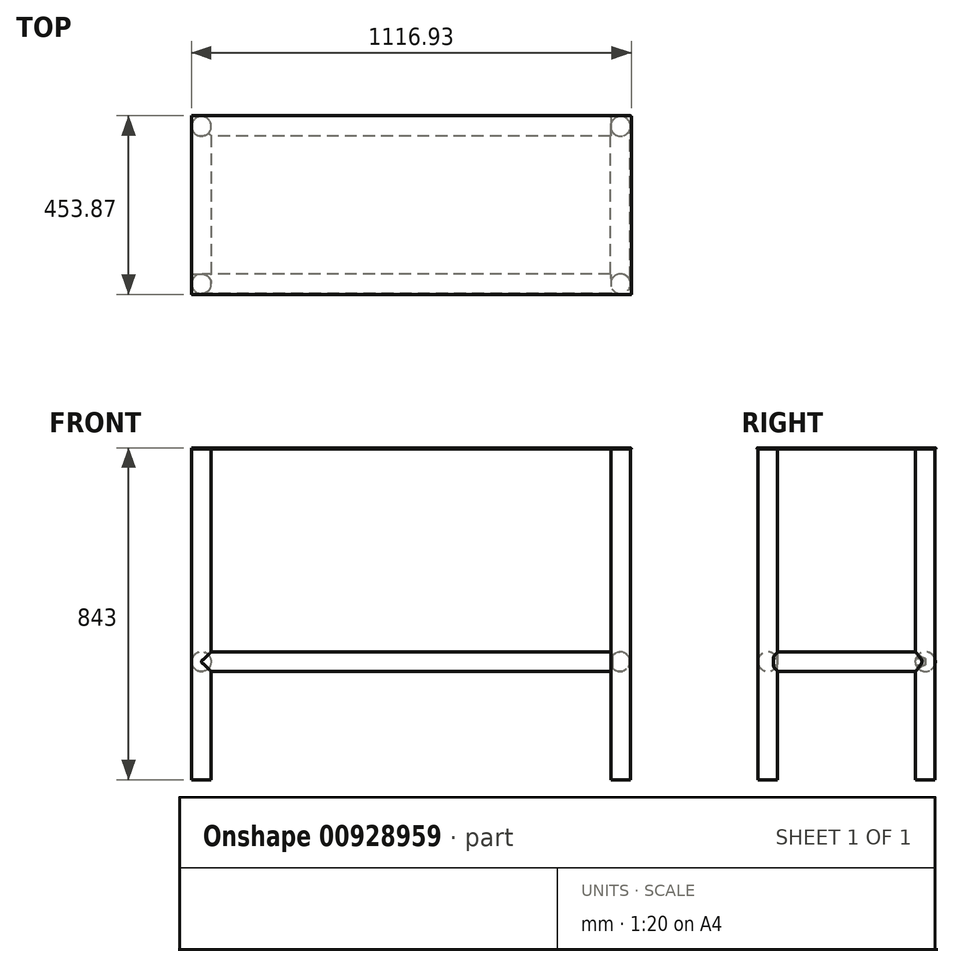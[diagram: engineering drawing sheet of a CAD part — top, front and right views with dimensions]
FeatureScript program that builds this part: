
annotation { "Feature Type Name" : "Feature", "Feature Type Description" : "" }
export const myFeature = defineFeature(function(context is Context, id is Id, definition is map)
    precondition{}
    {
        {
            var Q0;
            Q0=qCreatedBy(makeId("Top.planeOp"),FACE);
            var sketch = newSketch(context, id + "F0", { "sketchPlane" : qUnion([Q0])});
            skLineSegment(sketch, "E0", {"start": v(0, 359.04) * mm, "end": v(0, -402.62) * mm, "construction": true});
            skLineSegment(sketch, "E1", {"start": v(-459.46, 0) * mm, "end": v(421.57, 0) * mm, "construction": true});
            skCircle(sketch, "E2", {"center": v(-532.5, 200) * mm, "radius": 25 * mm});
            skCircle(sketch, "E3", {"center": v(-532.5, -200) * mm, "radius": 25 * mm});
            skCircle(sketch, "E4", {"center": v(532.5, 200) * mm, "radius": 25 * mm});
            skCircle(sketch, "E5", {"center": v(532.5, -200) * mm, "radius": 25 * mm});
            skSolve(sketch);
        }
        {
            var Q0;
            Q0 = qSketchRegion(id + "F0", true);
            extrude(context, id + "F1", {"entities" : qUnion([Q0]), "depth" : 840 * mm, "offsetDistance" : 25.4 * mm});
        }
        {
            var Q0;
            Q0=makeQuery(id+"F1.opExtrude","CAP_FACE",FACE,{"disambiguationData":[OSD([sQuery(id+"F0.wireOp",EDGE,"E2")])],"isStart":false});
            var sketch = newSketch(context, id + "F2", { "sketchPlane" : qUnion([Q0])});
            skLineSegment(sketch, "E6.bottom", {"start": v(-557.5, 225) * mm, "end": v(557.5, 225) * mm});
            skLineSegment(sketch, "E6.top", {"start": v(-557.5, -225) * mm, "end": v(557.5, -225) * mm});
            skLineSegment(sketch, "E6.left", {"start": v(-557.5, 225) * mm, "end": v(-557.5, -225) * mm});
            skLineSegment(sketch, "E6.right", {"start": v(557.5, 225) * mm, "end": v(557.5, -225) * mm});
            skSolve(sketch);
        }
        {
            var Q0;
            Q0 = qSketchRegion(id + "F2", true);
            extrude(context, id + "F3", {"entities" : qUnion([Q0]), "operationType" : NewBodyOperationType.ADD, "depth" : 3 * mm, "offsetDistance" : 25.4 * mm});
        }
        {
            var Q0;
            Q0=makeQuery(id+"F3.opExtrude","SWEPT_FACE",FACE,{"disambiguationData":[OSD([sQuery(id+"F2.wireOp",EDGE,"E6.left")])]});
            var sketch = newSketch(context, id + "F4", { "sketchPlane" : qUnion([Q0])});
            skArc(sketch, "E7", {"start": v(226.62, 840) * mm, "mid": v(226.7, 841.98) * mm, "end": v(225, 843) * mm});
            skLineSegment(sketch, "E8", {"start": v(225, 840) * mm, "end": v(226.62, 840) * mm});
            skArc(sketch, "E9.MirrorCS", {"start": v(-676.62, 840) * mm, "mid": v(-676.7, 841.98) * mm, "end": v(-675, 843) * mm});
            skLineSegment(sketch, "E10.MirrorCS", {"start": v(-675, 840) * mm, "end": v(-676.62, 840) * mm});
            skArc(sketch, "E11", {"start": v(-225, 843) * mm, "mid": v(-226.7, 841.98) * mm, "end": v(-226.6, 840) * mm});
            skLineSegment(sketch, "E12", {"start": v(-225, 843) * mm, "end": v(-225, 840) * mm});
            skLineSegment(sketch, "E13", {"start": v(-225, 840) * mm, "end": v(-226.6, 840) * mm});
            skSolve(sketch);
        }
        {
            var Q0;
            Q0=makeQuery(id+"F3.opExtrude","SWEPT_FACE",FACE,{"disambiguationData":[OSD([sQuery(id+"F2.wireOp",EDGE,"E6.top")])]});
            var sketch = newSketch(context, id + "F5", { "sketchPlane" : qUnion([Q0])});
            skArc(sketch, "E14", {"start": v(559.1, 840) * mm, "mid": v(559.2, 841.98) * mm, "end": v(557.5, 843) * mm});
            skLineSegment(sketch, "E15", {"start": v(557.5, 843) * mm, "end": v(557.5, 840) * mm});
            skLineSegment(sketch, "E16", {"start": v(557.5, 840) * mm, "end": v(559.1, 840) * mm});
            skSolve(sketch);
        }
        {
            var Q0;
            Q0 = qSketchRegion(id + "F4", true);
            var Q1;
            Q1=makeQuery(id+"F4.imprint","IMPRINT",FACE,{"disambiguationData":[TD([[makeQuery(id+"F4.imprint","IMPRINT",EDGE,{"derivedFrom":sQuery(id+"F4.wireOp",EDGE,"E7")}),1.0]])]});
            var Q2;
            Q2=makeQuery(id+"F3.opExtrude","SWEPT_FACE",FACE,{"disambiguationData":[OSD([sQuery(id+"F2.wireOp",EDGE,"E6.right")])]});
            extrude(context, id + "F6", {"entities" : qUnion([Q0, Q1]), "operationType" : NewBodyOperationType.ADD, "endBound" : BoundingType.UP_TO_SURFACE, "oppositeDirection" : true, "depth" : 25.4 * mm, "endBoundEntityFace" : qUnion([Q2]), "offsetDistance" : 25.4 * mm});
        }
        {
            var Q0;
            Q0=makeQuery(id+"F5.imprint","IMPRINT",FACE,{"disambiguationData":[TD([[makeQuery(id+"F5.imprint","IMPRINT",EDGE,{"derivedFrom":sQuery(id+"F5.wireOp",EDGE,"E14")}),1.0]])]});
            var Q1;
            Q1=makeQuery(id+"F6.opExtrude","CAP_VERTEX",VERTEX,{"disambiguationData":[OSD([sQuery(id+"F4.wireOp",EDGE,"E11"),sQuery(id+"F4.wireOp",EDGE,"E13")])],"isStart":false});
            var Q2;
            Q2=makeQuery(id+"F6.opExtrude","CAP_VERTEX",VERTEX,{"disambiguationData":[OSD([sQuery(id+"F4.wireOp",EDGE,"E7"),sQuery(id+"F4.wireOp",EDGE,"E8")])],"isStart":false});
            extrude(context, id + "F7", {"entities" : qUnion([Q0]), "operationType" : NewBodyOperationType.ADD, "endBound" : BoundingType.UP_TO_VERTEX, "oppositeDirection" : true, "depth" : 25.4 * mm, "endBoundEntityVertex" : qUnion([Q1]), "offsetDistance" : 25.4 * mm, "hasSecondDirection" : true, "secondDirectionBound" : SecondDirectionBoundingType.UP_TO_VERTEX, "secondDirectionOppositeDirection" : false, "secondDirectionDepth" : 25.4 * mm, "secondDirectionBoundEntityVertex" : qUnion([Q2])});
        }
        {
            var Q0;
            Q0=makeQuery(id+"F1.opExtrude","CAP_EDGE",EDGE,{"disambiguationData":[OSD([sQuery(id+"F0.wireOp",EDGE,"E3")])],"isStart":true});
            cPlane(context, id + "F8", {"entities" : qUnion([Q0]), "cplaneType" : CPlaneType.LINE_ANGLE, "offset" : 25.4 * mm, "angle" : 0 * degree, "width" : 152.4 * mm, "height" : 152.4 * mm});
        }
        {
            var Q0;
            Q0=qCreatedBy(id+"F8.planeOp",FACE);
            var sketch = newSketch(context, id + "F9", { "sketchPlane" : qUnion([Q0])});
            skCircle(sketch, "E17", {"center": v(-200.07, 300) * mm, "radius": 25 * mm});
            skSolve(sketch);
        }
        {
            var Q0;
            Q0 = qSketchRegion(id + "F9", true);
            extrude(context, id + "F10", {"entities" : qUnion([Q0]), "operationType" : NewBodyOperationType.ADD, "depth" : 1039.88 * mm, "offsetDistance" : 25.4 * mm});
        }
        {
            var Q0;
            Q0=makeQuery(id+"F1.opExtrude","CAP_EDGE",EDGE,{"disambiguationData":[OSD([sQuery(id+"F0.wireOp",EDGE,"E2")])],"isStart":true});
            cPlane(context, id + "F11", {"entities" : qUnion([Q0]), "cplaneType" : CPlaneType.LINE_ANGLE, "offset" : 25.4 * mm, "angle" : 0 * degree, "width" : 152.4 * mm, "height" : 152.4 * mm});
        }
        {
            var Q0;
            Q0=qCreatedBy(id+"F11.planeOp",FACE);
            var sketch = newSketch(context, id + "F12", { "sketchPlane" : qUnion([Q0])});
            skCircle(sketch, "E18", {"center": v(200.5, 300) * mm, "radius": 25 * mm});
            skSolve(sketch);
        }
        {
            var Q0;
            Q0 = qSketchRegion(id + "F12", true);
            extrude(context, id + "F13", {"entities" : qUnion([Q0]), "operationType" : NewBodyOperationType.ADD, "depth" : 1039.88 * mm, "offsetDistance" : 25.4 * mm});
        }
        {
            var Q0;
            Q0=makeQuery(id+"F1.opExtrude","CAP_EDGE",EDGE,{"disambiguationData":[OSD([sQuery(id+"F0.wireOp",EDGE,"E4")])],"isStart":true});
            cPlane(context, id + "F14", {"entities" : qUnion([Q0]), "cplaneType" : CPlaneType.LINE_ANGLE, "offset" : 25.4 * mm, "angle" : 90 * degree, "width" : 152.4 * mm, "height" : 152.4 * mm});
        }
        {
            var Q0;
            Q0=qCreatedBy(id+"F14.planeOp",FACE);
            var sketch = newSketch(context, id + "F15", { "sketchPlane" : qUnion([Q0])});
            skCircle(sketch, "E19", {"center": v(-531.08, 300) * mm, "radius": 25 * mm});
            skSolve(sketch);
        }
        {
            var Q0;
            Q0 = qSketchRegion(id + "F15", true);
            extrude(context, id + "F16", {"entities" : qUnion([Q0]), "operationType" : NewBodyOperationType.ADD, "oppositeDirection" : true, "depth" : 386.08 * mm, "offsetDistance" : 25.4 * mm});
        }
        {
            var Q0;
            Q0=makeQuery(id+"F1.opExtrude","CAP_EDGE",EDGE,{"disambiguationData":[OSD([sQuery(id+"F0.wireOp",EDGE,"E2")])],"isStart":true});
            cPlane(context, id + "F17", {"entities" : qUnion([Q0]), "cplaneType" : CPlaneType.LINE_ANGLE, "offset" : 25.4 * mm, "angle" : 90 * degree, "width" : 152.4 * mm, "height" : 152.4 * mm});
        }
        {
            var Q0;
            Q0=qCreatedBy(id+"F17.planeOp",FACE);
            var sketch = newSketch(context, id + "F18", { "sketchPlane" : qUnion([Q0])});
            skCircle(sketch, "E20", {"center": v(532.05, 300) * mm, "radius": 25 * mm});
            skSolve(sketch);
        }
        {
            var Q0;
            Q0 = qSketchRegion(id + "F18", true);
            extrude(context, id + "F19", {"entities" : qUnion([Q0]), "operationType" : NewBodyOperationType.ADD, "oppositeDirection" : true, "depth" : 374.9 * mm, "offsetDistance" : 25.4 * mm});
        }
    });
